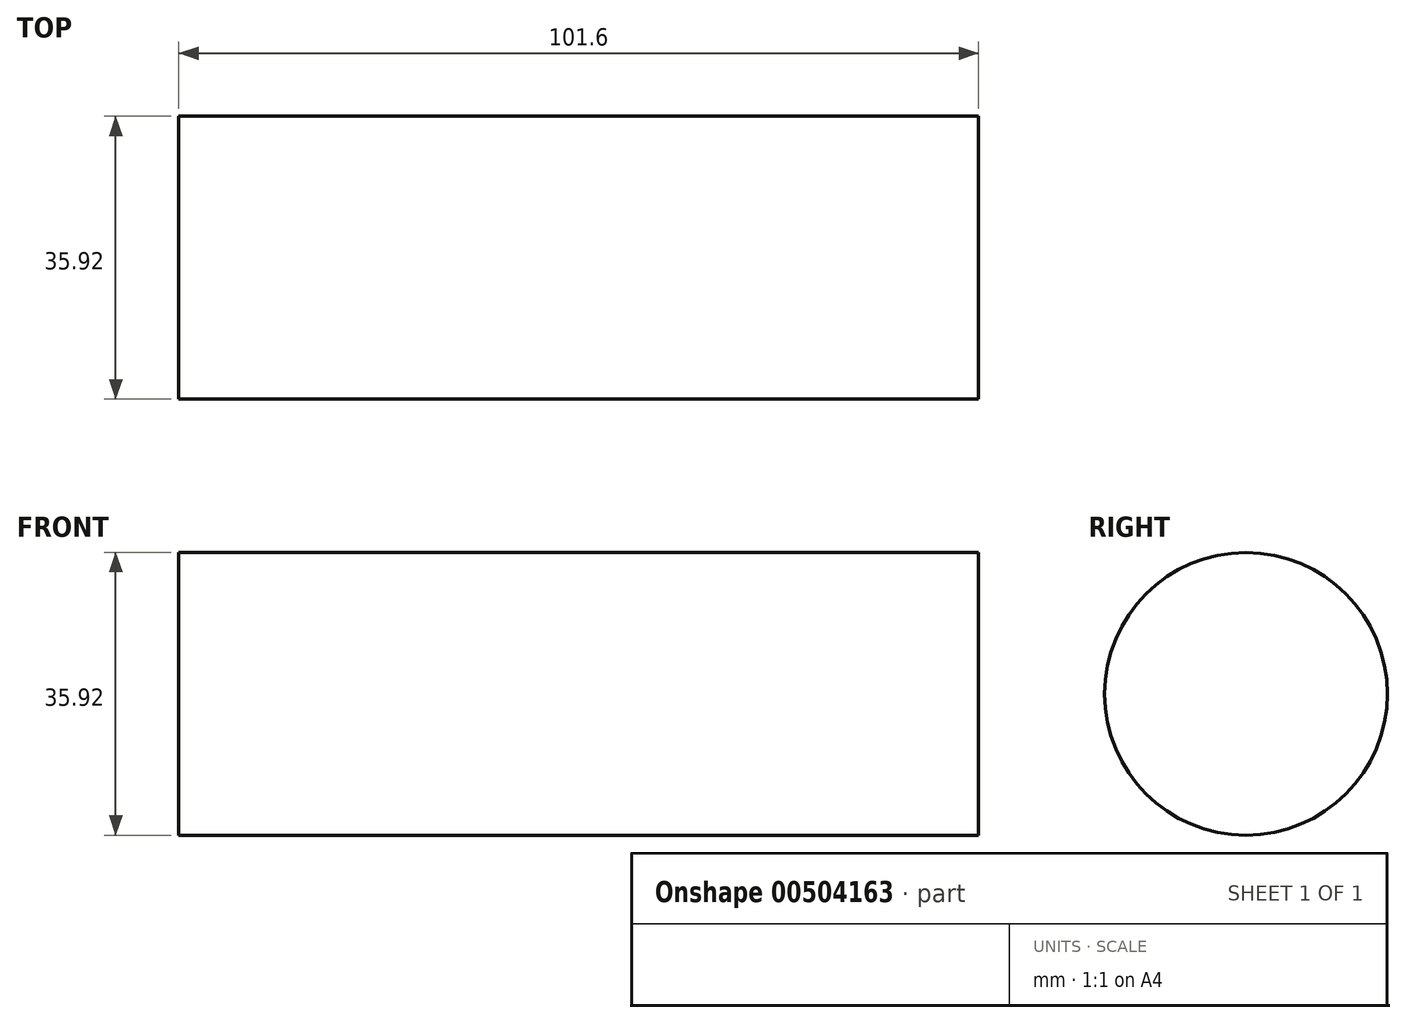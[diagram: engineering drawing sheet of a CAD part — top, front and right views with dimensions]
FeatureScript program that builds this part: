
annotation { "Feature Type Name" : "Feature", "Feature Type Description" : "" }
export const myFeature = defineFeature(function(context is Context, id is Id, definition is map)
    precondition{}
    {
        {
            var Q0;
            Q0=qCreatedBy(makeId("Right.planeOp"),FACE);
            var sketch = newSketch(context, id + "F0", { "sketchPlane" : qUnion([Q0])});
            skCircle(sketch, "E0", {"center": v(0, 0) * mm, "radius": 17.96 * mm});
            skSolve(sketch);
        }
        {
            var Q0;
            Q0 = qSketchRegion(id + "F0", true);
            extrude(context, id + "F1", {"entities" : qUnion([Q0]), "depth" : 101.6 * mm});
        }
    });
